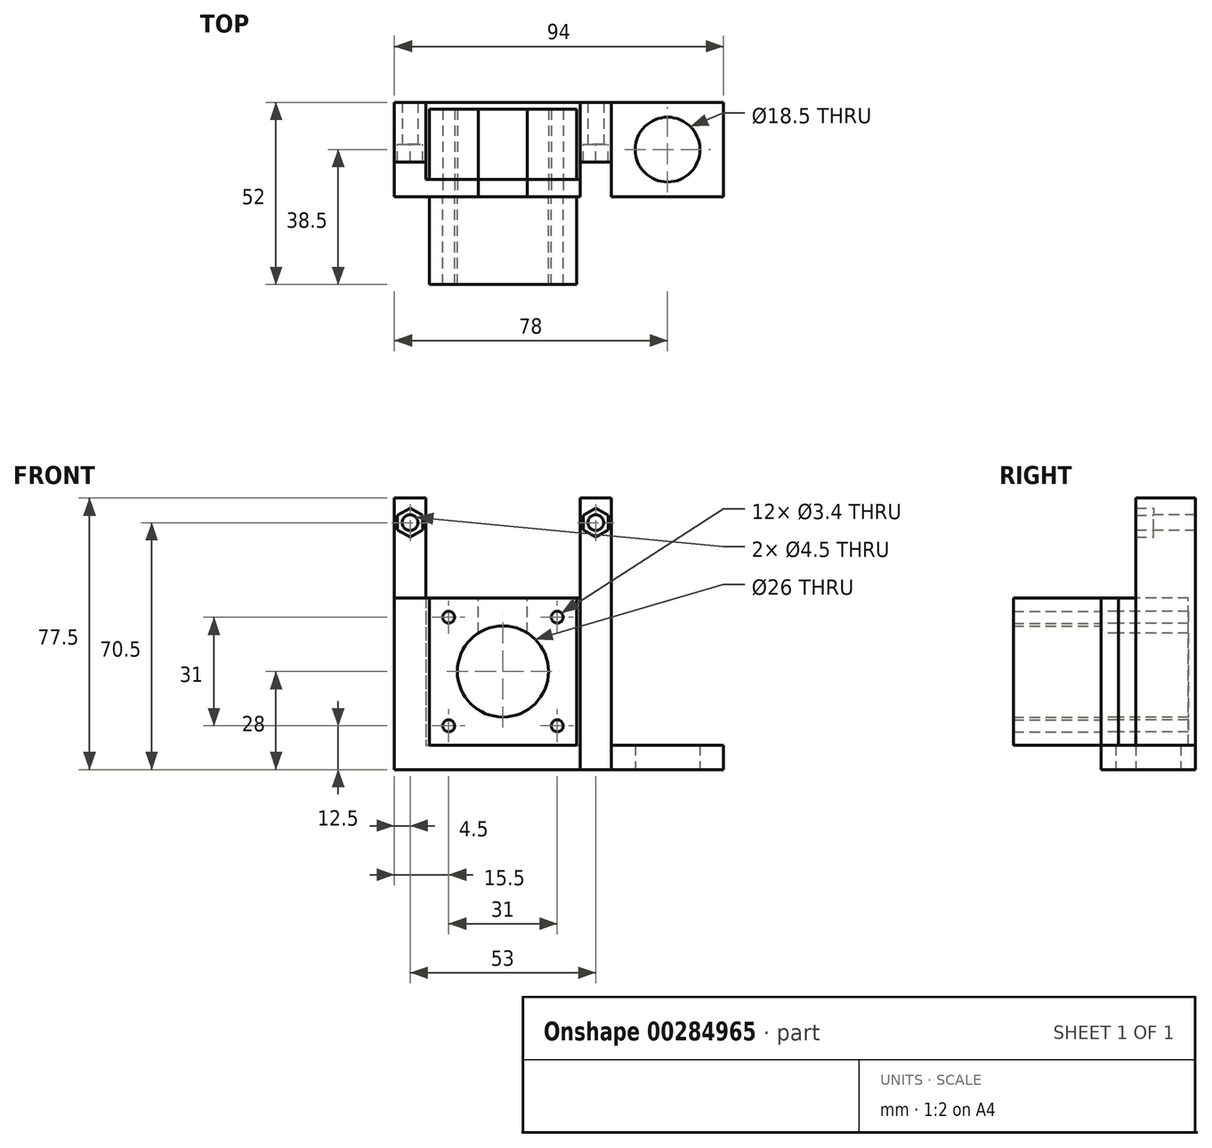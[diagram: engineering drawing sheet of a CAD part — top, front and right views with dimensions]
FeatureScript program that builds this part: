
annotation { "Feature Type Name" : "Feature", "Feature Type Description" : "" }
export const myFeature = defineFeature(function(context is Context, id is Id, definition is map)
    precondition{}
    {
        {
            assignVariable(context, id + "F0", {"name" : "MotorLength", "anyValue" : 20});
        }
        {
            var Q0;
            Q0=qCreatedBy(makeId("Front.planeOp"),FACE);
            var sketch = newSketch(context, id + "F1", { "sketchPlane" : qUnion([Q0])});
            skCircle(sketch, "E0", {"center": v(0, 0) * mm, "radius": 2.25 * mm});
            skCircle(sketch, "E1", {"center": v(-31.5, 49.5) * mm, "radius": 2.25 * mm});
            skCircle(sketch, "E2", {"center": v(21.5, 49.5) * mm, "radius": 2.25 * mm});
            skPoint(sketch, "E3", {"position": v(-36, 56.5) * mm});
            skPoint(sketch, "E4", {"position": v(-27, 56.5) * mm});
            skPoint(sketch, "E5", {"position": v(-27, -14) * mm});
            skLineSegment(sketch, "E6", {"start": v(-36, 56.5) * mm, "end": v(-27, 56.5) * mm});
            skLineSegment(sketch, "E7", {"start": v(-27, 56.5) * mm, "end": v(-27, -14) * mm});
            skLineSegment(sketch, "E8", {"start": v(-27, -14) * mm, "end": v(17, -14) * mm});
            skLineSegment(sketch, "E9", {"start": v(17, -14) * mm, "end": v(17, 56.5) * mm});
            skLineSegment(sketch, "E10", {"start": v(17, 56.5) * mm, "end": v(26, 56.5) * mm});
            skPoint(sketch, "E11", {"position": v(-36, -21) * mm});
            skLineSegment(sketch, "E12", {"start": v(-36, 56.5) * mm, "end": v(-36, -21) * mm});
            skLineSegment(sketch, "E13", {"start": v(-36, -21) * mm, "end": v(26, -21) * mm});
            skLineSegment(sketch, "E14", {"start": v(26, 56.5) * mm, "end": v(26, -21) * mm});
            skSolve(sketch);
        }
        {
            var Q0;
            Q0=makeQuery(id+"F1.imprint","IMPRINT",FACE,{"disambiguationData":[TD([[makeQuery(id+"F1.imprint","IMPRINT",EDGE,{"derivedFrom":sQuery(id+"F1.wireOp",EDGE,"E1")}),-1.0]])]});
            extrude(context, id + "F2", {"entities" : qUnion([Q0]), "oppositeDirection" : true, "depth" : 12 * mm});
        }
        {
            var Q0;
            Q0=makeQuery(id+"F2.opExtrude","CAP_FACE",FACE,{"disambiguationData":[OSD([sQuery(id+"F1.wireOp",EDGE,"E1"),sQuery(id+"F1.wireOp",EDGE,"E2"),sQuery(id+"F1.wireOp",EDGE,"E6"),sQuery(id+"F1.wireOp",EDGE,"E7"),sQuery(id+"F1.wireOp",EDGE,"E8"),sQuery(id+"F1.wireOp",EDGE,"E9"),sQuery(id+"F1.wireOp",EDGE,"E10"),sQuery(id+"F1.wireOp",EDGE,"E12"),sQuery(id+"F1.wireOp",EDGE,"E13"),sQuery(id+"F1.wireOp",EDGE,"E14")])],"isStart":true});
            var sketch = newSketch(context, id + "F3", { "sketchPlane" : qUnion([Q0])});
            skCircle(sketch, "E15.cCircle", {"center": v(-31.5, 49.5) * mm, "radius": 3.6 * mm, "construction": true});
            skLineSegment(sketch, "E15.0", {"start": v(-27.9, 51.58) * mm, "end": v(-27.9, 47.42) * mm});
            skLineSegment(sketch, "E15.1", {"start": v(-27.9, 47.42) * mm, "end": v(-31.5, 45.34) * mm});
            skLineSegment(sketch, "E15.2", {"start": v(-31.5, 45.34) * mm, "end": v(-35.1, 47.42) * mm});
            skLineSegment(sketch, "E15.3", {"start": v(-35.1, 47.42) * mm, "end": v(-35.1, 51.58) * mm});
            skLineSegment(sketch, "E15.4", {"start": v(-35.1, 51.58) * mm, "end": v(-31.5, 53.66) * mm});
            skLineSegment(sketch, "E15.5", {"start": v(-31.5, 53.66) * mm, "end": v(-27.9, 51.58) * mm});
            skPoint(sketch, "E15.0.midPoint", {"position": v(-27.9, 49.5) * mm});
            skCircle(sketch, "E16.cCircle", {"center": v(21.5, 49.5) * mm, "radius": 3.6 * mm, "construction": true});
            skLineSegment(sketch, "E16.0", {"start": v(25.1, 51.58) * mm, "end": v(25.1, 47.42) * mm});
            skLineSegment(sketch, "E16.1", {"start": v(25.1, 47.42) * mm, "end": v(21.5, 45.34) * mm});
            skLineSegment(sketch, "E16.2", {"start": v(21.5, 45.34) * mm, "end": v(17.9, 47.42) * mm});
            skLineSegment(sketch, "E16.3", {"start": v(17.9, 47.42) * mm, "end": v(17.9, 51.58) * mm});
            skLineSegment(sketch, "E16.4", {"start": v(17.9, 51.58) * mm, "end": v(21.5, 53.66) * mm});
            skLineSegment(sketch, "E16.5", {"start": v(21.5, 53.66) * mm, "end": v(25.1, 51.58) * mm});
            skPoint(sketch, "E16.0.midPoint", {"position": v(25.1, 49.5) * mm});
            skSolve(sketch);
        }
        {
            var Q0;
            Q0=makeQuery(id+"F3.imprint","IMPRINT",FACE,{"disambiguationData":[TD([[makeQuery(id+"F3.imprint","IMPRINT",EDGE,{"derivedFrom":sQuery(id+"F3.wireOp",EDGE,"E15.0")}),1.0]])]});
            extrude(context, id + "F4", {"entities" : qUnion([Q0]), "operationType" : NewBodyOperationType.ADD, "depth" : 5 * mm});
        }
        {
            var Q0;
            {var subQ0=sQuery(id+"F1.wireOp",EDGE,"E8");Q0=makeQuery(id+"F4.boolean.opBoolean","MERGE",FACE,{"derivedFrom":[makeQuery(id+"F2.opExtrude","SWEPT_FACE",FACE,{"disambiguationData":[OSD([subQ0])]}),makeQuery(id+"F4.opExtrude","SWEPT_FACE",FACE,{"disambiguationData":[OSD([subQ0])]})]});}
            var sketch = newSketch(context, id + "F5", { "sketchPlane" : qUnion([Q0])});
            skLineSegment(sketch, "E17.0", {"start": v(-27, 12) * mm, "end": v(17, 12) * mm});
            skPoint(sketch, "E18.oppositeSnap0", {"position": v(17, 3.5) * mm});
            skLineSegment(sketch, "E18.top", {"start": v(-27, -10) * mm, "end": v(17, -10) * mm});
            skLineSegment(sketch, "E18.left", {"start": v(-27, 12) * mm, "end": v(-27, -10) * mm});
            skLineSegment(sketch, "E18.right", {"start": v(17, 12) * mm, "end": v(17, -10) * mm});
            skLineSegment(sketch, "E19.top", {"start": v(-27, -15) * mm, "end": v(17, -15) * mm});
            skLineSegment(sketch, "E19.left", {"start": v(-27, -10) * mm, "end": v(-27, -15) * mm});
            skLineSegment(sketch, "E19.right", {"start": v(17, -10) * mm, "end": v(17, -15) * mm});
            skLineSegment(sketch, "E20.0", {"start": v(17, -5) * mm, "end": v(26, -5) * mm});
            skLineSegment(sketch, "E21.bottom", {"start": v(26, -5) * mm, "end": v(17, -5) * mm});
            skLineSegment(sketch, "E21.top", {"start": v(26, -15) * mm, "end": v(17, -15) * mm});
            skLineSegment(sketch, "E21.left", {"start": v(26, -5) * mm, "end": v(26, -15) * mm});
            skLineSegment(sketch, "E21.right", {"start": v(17, -5) * mm, "end": v(17, -15) * mm});
            skLineSegment(sketch, "E22.0", {"start": v(-36, -5) * mm, "end": v(-27, -5) * mm});
            skLineSegment(sketch, "E23.top", {"start": v(-36, -15) * mm, "end": v(-27, -15) * mm});
            skLineSegment(sketch, "E23.left", {"start": v(-36, -5) * mm, "end": v(-36, -15) * mm});
            skLineSegment(sketch, "E23.right", {"start": v(-27, -5) * mm, "end": v(-27, -15) * mm});
            skSolve(sketch);
        }
        {
            var Q0;
            {var subQ0=sQuery(id+"F5.wireOp",EDGE,"E18.top");Q0=makeQuery(id+"F5.imprint","IMPRINT",FACE,{"disambiguationData":[TD([[makeQuery(id+"F5.imprint","IMPRINT",EDGE,{"derivedFrom":subQ0}),1.0]])]});}
            var Q1;
            {var subQ0=sQuery(id+"F5.wireOp",EDGE,"E18.top");Q1=makeQuery(id+"F5.imprint","IMPRINT",FACE,{"disambiguationData":[TD([[makeQuery(id+"F5.imprint","IMPRINT",EDGE,{"derivedFrom":subQ0}),-1.0]])]});}
            var Q2;
            {var subQ1=sQuery(id+"F5.wireOp",EDGE,"E22.0");Q2=makeQuery(id+"F5.imprint","IMPRINT",FACE,{"disambiguationData":[TD([[makeQuery(id+"F5.imprint","IMPRINT",EDGE,{"derivedFrom":subQ1}),-1.0]])]});}
            var Q3;
            {var subQ1=sQuery(id+"F5.wireOp",EDGE,"E21.bottom");Q3=makeQuery(id+"F5.imprint","IMPRINT",FACE,{"disambiguationData":[TD([[makeQuery(id+"F5.imprint","IMPRINT",EDGE,{"derivedFrom":subQ1}),1.0]])]});}
            var Q4;
            {var subQ0=sQuery(id+"F1.wireOp",EDGE,"E13");Q4=makeQuery(id+"F4.boolean.opBoolean","MERGE",FACE,{"derivedFrom":[makeQuery(id+"F2.opExtrude","SWEPT_FACE",FACE,{"disambiguationData":[OSD([subQ0])]}),makeQuery(id+"F4.opExtrude","SWEPT_FACE",FACE,{"disambiguationData":[OSD([subQ0])]})]});}
            extrude(context, id + "F6", {"entities" : qUnion([Q0, Q1, Q2, Q3]), "operationType" : NewBodyOperationType.ADD, "endBound" : BoundingType.UP_TO_SURFACE, "oppositeDirection" : true, "endBoundEntityFace" : qUnion([Q4]), "depth" : 25 * mm});
        }
        {
            var Q0;
            {var subQ0=sQuery(id+"F5.wireOp",EDGE,"E18.top");Q0=makeQuery(id+"F5.imprint","IMPRINT",FACE,{"disambiguationData":[TD([[makeQuery(id+"F5.imprint","IMPRINT",EDGE,{"derivedFrom":subQ0}),-1.0]])]});}
            var Q1;
            {var subQ1=sQuery(id+"F5.wireOp",EDGE,"E22.0");Q1=makeQuery(id+"F5.imprint","IMPRINT",FACE,{"disambiguationData":[TD([[makeQuery(id+"F5.imprint","IMPRINT",EDGE,{"derivedFrom":subQ1}),-1.0]])]});}
            var Q2;
            {var subQ1=sQuery(id+"F5.wireOp",EDGE,"E21.bottom");Q2=makeQuery(id+"F5.imprint","IMPRINT",FACE,{"disambiguationData":[TD([[makeQuery(id+"F5.imprint","IMPRINT",EDGE,{"derivedFrom":subQ1}),1.0]])]});}
            extrude(context, id + "F7", {"entities" : qUnion([Q0, Q1, Q2]), "operationType" : NewBodyOperationType.ADD, "depth" : 42 * mm});
        }
        {
            var Q0;
            {var subQ0=sQuery(id+"F5.wireOp",EDGE,"E23.top");var subQ1=sQuery(id+"F5.wireOp",EDGE,"E21.top");var subQ2=sQuery(id+"F5.wireOp",EDGE,"E19.top");Q0=makeQuery(id+"F7.boolean.opBoolean","MERGE",FACE,{"derivedFrom":[makeQuery(id+"F6.opExtrude","SWEPT_FACE",FACE,{"disambiguationData":[OSD([subQ2,subQ1,subQ0])]}),makeQuery(id+"F7.opExtrude","SWEPT_FACE",FACE,{"disambiguationData":[OSD([subQ2,subQ1,subQ0])]})]});}
            var sketch = newSketch(context, id + "F8", { "sketchPlane" : qUnion([Q0])});
            skLineSegment(sketch, "E24.0", {"start": v(-26, -14) * mm, "end": v(16, -14) * mm});
            skPoint(sketch, "E25", {"position": v(-5, -14) * mm});
            skPoint(sketch, "E26", {"position": v(-26, -14) * mm});
            skPoint(sketch, "E27", {"position": v(16, -14) * mm});
            skPoint(sketch, "E28.orphan", {"position": v(-27, -14) * mm});
            skPoint(sketch, "E29.orphan", {"position": v(17, -14) * mm});
            skPoint(sketch, "E30", {"position": v(-26, 28) * mm});
            skPoint(sketch, "E31", {"position": v(16, 28) * mm});
            skLineSegment(sketch, "E32", {"start": v(-26, 28) * mm, "end": v(16, -14) * mm, "construction": true});
            skLineSegment(sketch, "E33", {"start": v(-26, -14) * mm, "end": v(16, 28) * mm, "construction": true});
            skPoint(sketch, "E34", {"position": v(-5, 7) * mm});
            skCircle(sketch, "E35", {"center": v(-5, 7) * mm, "radius": 13 * mm});
            skCircle(sketch, "E36", {"center": v(-20.5, 22.5) * mm, "radius": 1.7 * mm});
            skCircle(sketch, "E37.1.0", {"center": v(-20.5, -8.5) * mm, "radius": 1.7 * mm});
            skCircle(sketch, "E37.2.0", {"center": v(10.5, -8.5) * mm, "radius": 1.7 * mm});
            skCircle(sketch, "E37.3.0", {"center": v(10.5, 22.5) * mm, "radius": 1.7 * mm});
            skSolve(sketch);
        }
        {
            var Q0;
            Q0=makeQuery(id+"F8.imprint","IMPRINT",FACE,{"disambiguationData":[TD([[makeQuery(id+"F8.imprint","IMPRINT",EDGE,{"derivedFrom":sQuery(id+"F8.wireOp",EDGE,"E36")}),1.0]])]});
            var Q1;
            Q1=makeQuery(id+"F8.imprint","IMPRINT",FACE,{"disambiguationData":[TD([[makeQuery(id+"F8.imprint","IMPRINT",EDGE,{"derivedFrom":sQuery(id+"F8.wireOp",EDGE,"E35")}),1.0]])]});
            var Q2;
            Q2=makeQuery(id+"F8.imprint","IMPRINT",FACE,{"disambiguationData":[TD([[makeQuery(id+"F8.imprint","IMPRINT",EDGE,{"derivedFrom":sQuery(id+"F8.wireOp",EDGE,"E37.1.0")}),1.0]])]});
            var Q3;
            Q3=makeQuery(id+"F8.imprint","IMPRINT",FACE,{"disambiguationData":[TD([[makeQuery(id+"F8.imprint","IMPRINT",EDGE,{"derivedFrom":sQuery(id+"F8.wireOp",EDGE,"E37.2.0")}),1.0]])]});
            var Q4;
            Q4=makeQuery(id+"F8.imprint","IMPRINT",FACE,{"disambiguationData":[TD([[makeQuery(id+"F8.imprint","IMPRINT",EDGE,{"derivedFrom":sQuery(id+"F8.wireOp",EDGE,"E37.3.0")}),1.0]])]});
            var Q5;
            Q5=makeQuery(id+"F7.opExtrude","SWEPT_FACE",FACE,{"disambiguationData":[OSD([sQuery(id+"F5.wireOp",EDGE,"E18.top")])]});
            extrude(context, id + "F9", {"entities" : qUnion([Q0, Q1, Q2, Q3, Q4]), "operationType" : NewBodyOperationType.REMOVE, "endBound" : BoundingType.UP_TO_SURFACE, "oppositeDirection" : true, "endBoundEntityFace" : qUnion([Q5]), "depth" : 25 * mm});
        }
        {
            var Q0;
            Q0=makeQuery(id+"F7.opExtrude","CAP_FACE",FACE,{"disambiguationData":[OSD([sQuery(id+"F5.wireOp",EDGE,"E18.top"),sQuery(id+"F5.wireOp",EDGE,"E19.top"),sQuery(id+"F5.wireOp",EDGE,"E21.bottom"),sQuery(id+"F5.wireOp",EDGE,"E21.top"),sQuery(id+"F5.wireOp",EDGE,"E21.left"),sQuery(id+"F5.wireOp",EDGE,"E21.right"),sQuery(id+"F5.wireOp",EDGE,"E22.0"),sQuery(id+"F5.wireOp",EDGE,"E23.top"),sQuery(id+"F5.wireOp",EDGE,"E23.left"),sQuery(id+"F5.wireOp",EDGE,"E23.right")])],"isStart":false});
            var sketch = newSketch(context, id + "F10", { "sketchPlane" : qUnion([Q0])});
            skLineSegment(sketch, "E38", {"start": v(-5, -15) * mm, "end": v(-5, -10) * mm, "construction": true});
            skLineSegment(sketch, "E39", {"start": v(-5, -10) * mm, "end": v(-12, -10) * mm});
            skLineSegment(sketch, "E40", {"start": v(-5, -10) * mm, "end": v(2, -10) * mm});
            skLineSegment(sketch, "E41.bottom", {"start": v(-12, -10) * mm, "end": v(2, -10) * mm});
            skLineSegment(sketch, "E41.top", {"start": v(-12, -15) * mm, "end": v(2, -15) * mm});
            skLineSegment(sketch, "E41.left", {"start": v(-12, -10) * mm, "end": v(-12, -15) * mm});
            skLineSegment(sketch, "E41.right", {"start": v(2, -10) * mm, "end": v(2, -15) * mm});
            skSolve(sketch);
        }
        {
            var Q0;
            Q0=makeQuery(id+"F10.imprint","IMPRINT",FACE,{"disambiguationData":[TD([[makeQuery(id+"F10.imprint","IMPRINT",EDGE,{"derivedFrom":sQuery(id+"F10.wireOp",EDGE,"E41.top")}),1.0]])]});
            var Q1;
            Q1=makeQuery(id+"F9.boolean.opBoolean","COPY",FACE,{"derivedFrom":makeQuery(id+"F9.opExtrude","SWEPT_FACE",FACE,{"disambiguationData":[OSD([sQuery(id+"F8.wireOp",EDGE,"E35")])]})});
            extrude(context, id + "F11", {"entities" : qUnion([Q0]), "operationType" : NewBodyOperationType.REMOVE, "endBound" : BoundingType.UP_TO_SURFACE, "oppositeDirection" : true, "endBoundEntityFace" : qUnion([Q1]), "depth" : 25 * mm});
        }
        {
            var Q0;
            Q0=makeQuery(id+"F7.opExtrude","SWEPT_FACE",FACE,{"disambiguationData":[OSD([sQuery(id+"F5.wireOp",EDGE,"E18.top")])]});
            var sketch = newSketch(context, id + "F12", { "sketchPlane" : qUnion([Q0])});
            skLineSegment(sketch, "E42.0", {"start": v(26, -14) * mm, "end": v(-16, -14) * mm});
            skLineSegment(sketch, "E43", {"start": v(-16, -14) * mm, "end": v(-16, 28) * mm});
            skLineSegment(sketch, "E44", {"start": v(-16, 28) * mm, "end": v(26, 28) * mm});
            skLineSegment(sketch, "E45", {"start": v(26, 28) * mm, "end": v(26, -14) * mm});
            skSolve(sketch);
        }
        {
            var Q0;
            Q0=makeQuery(id+"F12.imprint","IMPRINT",FACE,{"disambiguationData":[TD([[makeQuery(id+"F12.imprint","IMPRINT",EDGE,{"derivedFrom":sQuery(id+"F12.wireOp",EDGE,"E42.0")}),-1.0]])]});
            var Q1;
            Q1=makeQuery(id+"F12.imprint","IMPRINT",FACE,{"disambiguationData":[TD([[makeQuery(id+"F12.imprint","IMPRINT",EDGE,{"derivedFrom":makeQuery(id+"F9.boolean.opBoolean","COPY",EDGE,{"derivedFrom":makeQuery(id+"F9.opExtrude","CAP_EDGE",EDGE,{"disambiguationData":[OSD([sQuery(id+"F8.wireOp",EDGE,"E35")])],"isStart":false})})}),-1.0]])]});
            var Q2;
            Q2=makeQuery(id+"F12.imprint","IMPRINT",FACE,{"disambiguationData":[TD([[makeQuery(id+"F12.imprint","IMPRINT",EDGE,{"derivedFrom":makeQuery(id+"F9.boolean.opBoolean","COPY",EDGE,{"derivedFrom":makeQuery(id+"F9.opExtrude","CAP_EDGE",EDGE,{"disambiguationData":[OSD([sQuery(id+"F8.wireOp",EDGE,"E36")])],"isStart":false})})}),-1.0]])]});
            var Q3;
            Q3=makeQuery(id+"F12.imprint","IMPRINT",FACE,{"disambiguationData":[TD([[makeQuery(id+"F12.imprint","IMPRINT",EDGE,{"derivedFrom":makeQuery(id+"F9.boolean.opBoolean","COPY",EDGE,{"derivedFrom":makeQuery(id+"F9.opExtrude","CAP_EDGE",EDGE,{"disambiguationData":[OSD([sQuery(id+"F8.wireOp",EDGE,"E37.3.0")])],"isStart":false})})}),-1.0]])]});
            var Q4;
            Q4=makeQuery(id+"F12.imprint","IMPRINT",FACE,{"disambiguationData":[TD([[makeQuery(id+"F12.imprint","IMPRINT",EDGE,{"derivedFrom":makeQuery(id+"F9.boolean.opBoolean","COPY",EDGE,{"derivedFrom":makeQuery(id+"F9.opExtrude","CAP_EDGE",EDGE,{"disambiguationData":[OSD([sQuery(id+"F8.wireOp",EDGE,"E37.2.0")])],"isStart":false})})}),-1.0]])]});
            var Q5;
            Q5=makeQuery(id+"F12.imprint","IMPRINT",FACE,{"disambiguationData":[TD([[makeQuery(id+"F12.imprint","IMPRINT",EDGE,{"derivedFrom":makeQuery(id+"F9.boolean.opBoolean","COPY",EDGE,{"derivedFrom":makeQuery(id+"F9.opExtrude","CAP_EDGE",EDGE,{"disambiguationData":[OSD([sQuery(id+"F8.wireOp",EDGE,"E37.1.0")])],"isStart":false})})}),-1.0]])]});
            extrude(context, id + "F13", {"entities" : qUnion([Q0, Q1, Q2, Q3, Q4, Q5]), "depth" : (getVariable(context, 'MotorLength')) * mm});
        }
        {
            var Q0;
            Q0=makeQuery(id+"F8.imprint","IMPRINT",FACE,{"disambiguationData":[TD([[makeQuery(id+"F8.imprint","IMPRINT",EDGE,{"derivedFrom":sQuery(id+"F8.wireOp",EDGE,"E35")}),-1.0]])]});
            var sketch = newSketch(context, id + "F14", { "sketchPlane" : qUnion([Q0])});
            skLineSegment(sketch, "E46.0", {"start": v(-26, 28) * mm, "end": v(16, -14) * mm, "construction": true});
            skLineSegment(sketch, "E47.0", {"start": v(-26, -14) * mm, "end": v(16, 28) * mm, "construction": true});
            skLineSegment(sketch, "E48.bottom", {"start": v(-26, 28) * mm, "end": v(16, 28) * mm});
            skLineSegment(sketch, "E48.top", {"start": v(-26, -14) * mm, "end": v(16, -14) * mm});
            skLineSegment(sketch, "E48.left", {"start": v(-26, 28) * mm, "end": v(-26, -14) * mm});
            skLineSegment(sketch, "E48.right", {"start": v(16, 28) * mm, "end": v(16, -14) * mm});
            skSolve(sketch);
        }
        {
            var Q0;
            Q0=makeQuery(id+"F14.imprint","IMPRINT",FACE,{"disambiguationData":[TD([[makeQuery(id+"F14.imprint","IMPRINT",EDGE,{"derivedFrom":sQuery(id+"F14.wireOp",EDGE,"E48.bottom")}),-1.0]])]});
            var Q1;
            Q1=makeQuery(id+"F8.imprint","IMPRINT",FACE,{"disambiguationData":[TD([[makeQuery(id+"F8.imprint","IMPRINT",EDGE,{"derivedFrom":sQuery(id+"F8.wireOp",EDGE,"E36")}),1.0]])]});
            var Q2;
            Q2=makeQuery(id+"F8.imprint","IMPRINT",FACE,{"disambiguationData":[TD([[makeQuery(id+"F8.imprint","IMPRINT",EDGE,{"derivedFrom":sQuery(id+"F8.wireOp",EDGE,"E35")}),1.0]])]});
            var Q3;
            Q3=makeQuery(id+"F8.imprint","IMPRINT",FACE,{"disambiguationData":[TD([[makeQuery(id+"F8.imprint","IMPRINT",EDGE,{"derivedFrom":sQuery(id+"F8.wireOp",EDGE,"E37.1.0")}),1.0]])]});
            var Q4;
            Q4=makeQuery(id+"F8.imprint","IMPRINT",FACE,{"disambiguationData":[TD([[makeQuery(id+"F8.imprint","IMPRINT",EDGE,{"derivedFrom":sQuery(id+"F8.wireOp",EDGE,"E37.3.0")}),1.0]])]});
            var Q5;
            Q5=makeQuery(id+"F8.imprint","IMPRINT",FACE,{"disambiguationData":[TD([[makeQuery(id+"F8.imprint","IMPRINT",EDGE,{"derivedFrom":sQuery(id+"F8.wireOp",EDGE,"E37.2.0")}),1.0]])]});
            extrude(context, id + "F15", {"entities" : qUnion([Q0, Q1, Q2, Q3, Q4, Q5]), "depth" : 25 * mm});
        }
        {
            var Q0;
            {var subQ0=sQuery(id+"F1.wireOp",EDGE,"E13");Q0=makeQuery(id+"F6.boolean.opBoolean","MERGE",FACE,{"derivedFrom":[makeQuery(id+"F4.boolean.opBoolean","MERGE",FACE,{"derivedFrom":[makeQuery(id+"F2.opExtrude","SWEPT_FACE",FACE,{"disambiguationData":[OSD([subQ0])]}),makeQuery(id+"F4.opExtrude","SWEPT_FACE",FACE,{"disambiguationData":[OSD([subQ0])]})]}),makeQuery(id+"F6.opExtrude","CAP_FACE",FACE,{"disambiguationData":[OSD([sQuery(id+"F1.wireOp",EDGE,"E8"),sQuery(id+"F5.wireOp",EDGE,"E19.top"),sQuery(id+"F5.wireOp",EDGE,"E21.bottom"),sQuery(id+"F5.wireOp",EDGE,"E21.top"),sQuery(id+"F5.wireOp",EDGE,"E21.left"),sQuery(id+"F5.wireOp",EDGE,"E22.0"),sQuery(id+"F5.wireOp",EDGE,"E23.top"),sQuery(id+"F5.wireOp",EDGE,"E23.left")])],"isStart":false})]});}
            var sketch = newSketch(context, id + "F16", { "sketchPlane" : qUnion([Q0])});
            skLineSegment(sketch, "E49.bottom", {"start": v(26, -12) * mm, "end": v(58, -12) * mm});
            skLineSegment(sketch, "E49.top", {"start": v(26, 15) * mm, "end": v(58, 15) * mm});
            skLineSegment(sketch, "E49.left", {"start": v(26, -12) * mm, "end": v(26, 15) * mm});
            skLineSegment(sketch, "E49.right", {"start": v(58, -12) * mm, "end": v(58, 15) * mm});
            skCircle(sketch, "E50", {"center": v(42, 1.5) * mm, "radius": 9.25 * mm});
            skPoint(sketch, "E50.centerSnap0", {"position": v(42, -12) * mm});
            skPoint(sketch, "E50.centerSnap1", {"position": v(26, 1.5) * mm});
            skLineSegment(sketch, "E51.0", {"start": v(-26, 40) * mm, "end": v(-26, 15) * mm, "construction": true});
            skLineSegment(sketch, "E52.0", {"start": v(-26, 15) * mm, "end": v(16, 15) * mm, "construction": true});
            skLineSegment(sketch, "E53", {"start": v(-5, 15) * mm, "end": v(-5, 40) * mm, "construction": true});
            skLineSegment(sketch, "E54", {"start": v(6.1, 15) * mm, "end": v(6.1, 40) * mm, "construction": true});
            skPoint(sketch, "E55", {"position": v(6.1, 27.5) * mm});
            skSolve(sketch);
        }
        {
            var Q0;
            Q0=qSketchRegion(id+"F16",true);
            var Q1;
            {var subQ0=sQuery(id+"F1.wireOp",EDGE,"E8");Q1=makeQuery(id+"F6.boolean.opBoolean","MERGE",FACE,{"derivedFrom":[makeQuery(id+"F4.boolean.opBoolean","MERGE",FACE,{"derivedFrom":[makeQuery(id+"F2.opExtrude","SWEPT_FACE",FACE,{"disambiguationData":[OSD([subQ0])]}),makeQuery(id+"F4.opExtrude","SWEPT_FACE",FACE,{"disambiguationData":[OSD([subQ0])]})]}),makeQuery(id+"F6.opExtrude","CAP_FACE",FACE,{"disambiguationData":[OSD([subQ0,sQuery(id+"F5.wireOp",EDGE,"E19.top"),sQuery(id+"F5.wireOp",EDGE,"E21.bottom"),sQuery(id+"F5.wireOp",EDGE,"E21.top"),sQuery(id+"F5.wireOp",EDGE,"E21.left"),sQuery(id+"F5.wireOp",EDGE,"E22.0"),sQuery(id+"F5.wireOp",EDGE,"E23.top"),sQuery(id+"F5.wireOp",EDGE,"E23.left")])],"isStart":true})]});}
            extrude(context, id + "F17", {"entities" : qUnion([Q0]), "endBound" : BoundingType.UP_TO_SURFACE, "oppositeDirection" : true, "endBoundEntityFace" : qUnion([Q1]), "depth" : 25 * mm});
        }
    });
